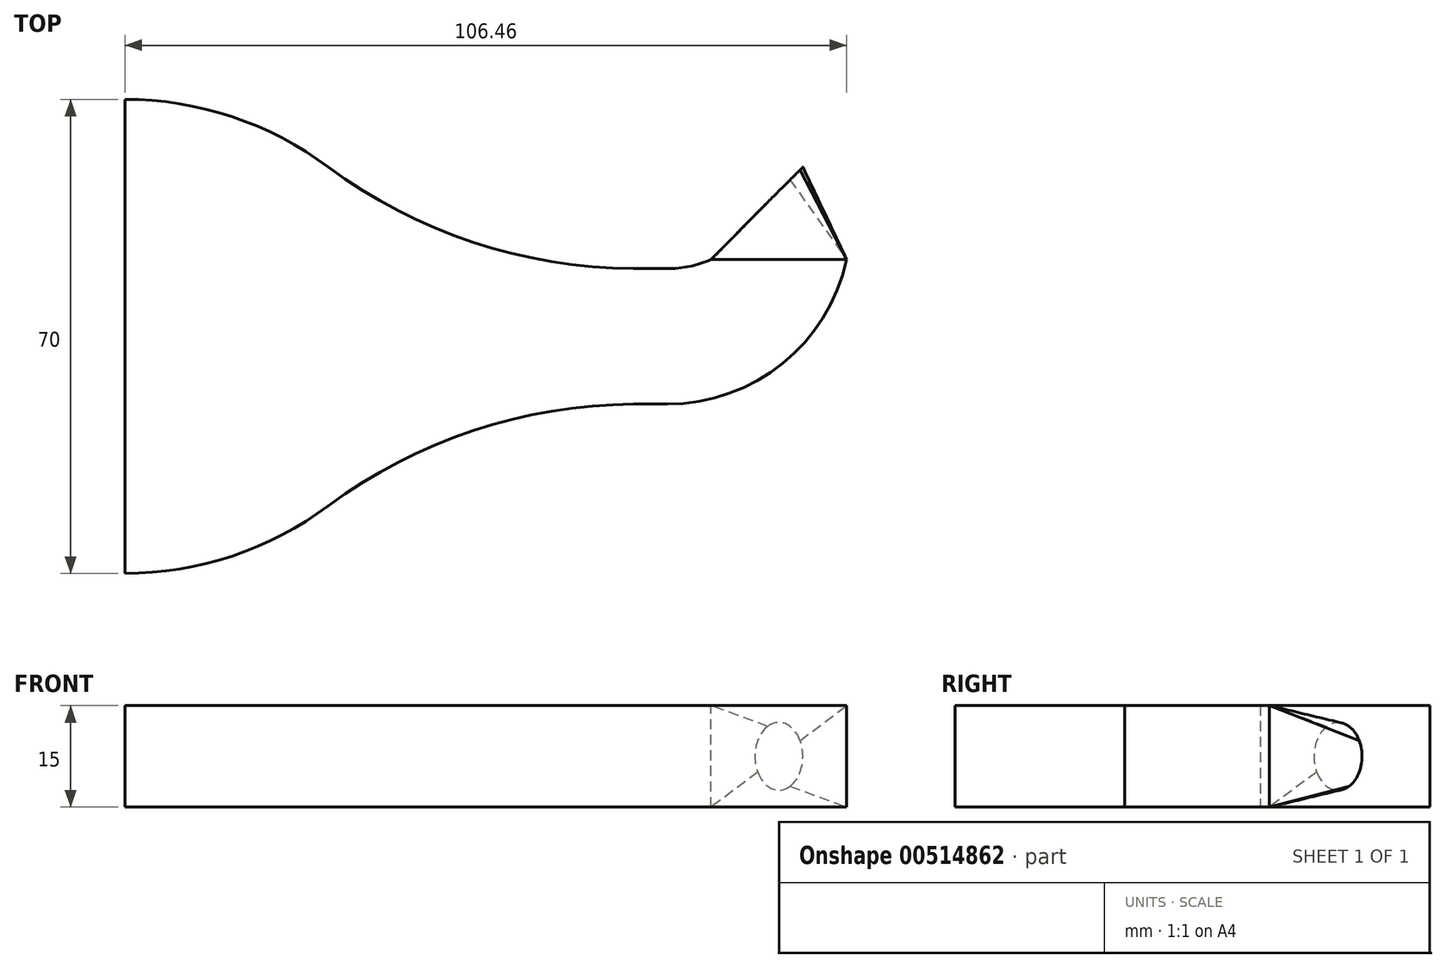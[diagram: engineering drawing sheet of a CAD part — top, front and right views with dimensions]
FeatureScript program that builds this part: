
annotation { "Feature Type Name" : "Feature", "Feature Type Description" : "" }
export const myFeature = defineFeature(function(context is Context, id is Id, definition is map)
    precondition{}
    {
        {
            var Q0;
            Q0=qCreatedBy(makeId("Top.planeOp"),FACE);
            var sketch = newSketch(context, id + "F0", { "sketchPlane" : qUnion([Q0])});
            skLineSegment(sketch, "E0.left", {"start": v(-50, 50) * mm, "end": v(-50, -50) * mm});
            skPoint(sketch, "E0.middle", {"position": v(0, 0) * mm});
            skLineSegment(sketch, "E1", {"start": v(-50, 50) * mm, "end": v(-50, 40) * mm});
            skLineSegment(sketch, "E2", {"start": v(50, 40) * mm, "end": v(42.93, 32.93) * mm});
            skLineSegment(sketch, "E3", {"start": v(42.93, 32.93) * mm, "end": v(46.46, 36.46) * mm});
            skLineSegment(sketch, "E4", {"start": v(-50, 0) * mm, "end": v(-50, -10) * mm});
            skLineSegment(sketch, "E5", {"start": v(-50, -10) * mm, "end": v(-50, 15) * mm});
            skLineSegment(sketch, "E6", {"start": v(-50, 15) * mm, "end": v(114.78, 15) * mm});
            skLineSegment(sketch, "E7", {"start": v(42.93, 32.93) * mm, "end": v(42.93, -37.04) * mm});
            skLineSegment(sketch, "E8", {"start": v(-50, 15) * mm, "end": v(30, 15) * mm});
            skLineSegment(sketch, "E9", {"start": v(30, 15) * mm, "end": v(30, 30) * mm});
            skLineSegment(sketch, "E10", {"start": v(30, 15) * mm, "end": v(30, 0) * mm});
            skLineSegment(sketch, "E11", {"start": v(42.93, 32.93) * mm, "end": v(81, 32.93) * mm});
            skLineSegment(sketch, "E12", {"start": v(46.46, 36.46) * mm, "end": v(46.46, 32.93) * mm});
            skLineSegment(sketch, "E13", {"start": v(46.46, 36.46) * mm, "end": v(46.46, 0) * mm});
            skLineSegment(sketch, "E14", {"start": v(46.46, 36.46) * mm, "end": v(62.14, 20.79) * mm});
            skLineSegment(sketch, "E15", {"start": v(-50, 50) * mm, "end": v(-109.66, 50) * mm});
            skLineSegment(sketch, "E16", {"start": v(-50, 40) * mm, "end": v(-110.5, 40) * mm});
            skLineSegment(sketch, "E17", {"start": v(-50, 15) * mm, "end": v(-113.83, 15) * mm});
            skLineSegment(sketch, "E18", {"start": v(-50, 0) * mm, "end": v(-113, 0) * mm});
            skLineSegment(sketch, "E19", {"start": v(-50, -10) * mm, "end": v(-113, -10) * mm});
            skLineSegment(sketch, "E20", {"start": v(-50, -50) * mm, "end": v(-111.33, -50) * mm});
            skLineSegment(sketch, "E21", {"start": v(30, 30) * mm, "end": v(95.7, 30) * mm});
            skPoint(sketch, "E22", {"position": v(42.93, 30) * mm});
            skPoint(sketch, "E23", {"position": v(46.46, 30) * mm});
            skPoint(sketch, "E24", {"position": v(42.93, 26.34) * mm});
            skLineSegment(sketch, "E25", {"start": v(30, 15) * mm, "end": v(30, 7.5) * mm});
            skLineSegment(sketch, "E26", {"start": v(30, 15) * mm, "end": v(30, 22.5) * mm});
            skLineSegment(sketch, "E27", {"start": v(30, 15) * mm, "end": v(0, 15) * mm});
            skLineSegment(sketch, "E28", {"start": v(-50, 15) * mm, "end": v(-30, 15) * mm});
            skLineSegment(sketch, "E29", {"start": v(-30, 15) * mm, "end": v(-10, 15) * mm});
            skLineSegment(sketch, "E30", {"start": v(-10, 15) * mm, "end": v(10, 15) * mm});
            skSolve(sketch);
        }
        {
            var Q0;
            Q0=sQuery(id+"F0.wireOp",EDGE,"E2");
            cPlane(context, id + "F1", {"entities" : qUnion([Q0]), "cplaneType" : CPlaneType.LINE_ANGLE, "offset" : 25 * mm, "angle" : 90 * degree, "width" : 150 * mm, "height" : 150 * mm});
        }
        {
            var Q0;
            Q0=qCreatedBy(id+"F1.planeOp",FACE);
            var sketch = newSketch(context, id + "F2", { "sketchPlane" : qUnion([Q0])});
            skCircle(sketch, "E31", {"center": v(58.64, 0) * mm, "radius": 5 * mm});
            skSolve(sketch);
        }
        {
            var Q0;
            Q0=sQuery(id+"F0.wireOp",VERTEX,"E6.start");
            var Q1;
            Q1=qCreatedBy(makeId("Right.planeOp"),FACE);
            cPlane(context, id + "F3", {"entities" : qUnion([Q0, Q1]), "cplaneType" : CPlaneType.PLANE_POINT, "offset" : 25 * mm, "width" : 150 * mm, "height" : 150 * mm});
        }
        {
            var Q0;
            Q0=qCreatedBy(id+"F3.planeOp",FACE);
            var sketch = newSketch(context, id + "F4", { "sketchPlane" : qUnion([Q0])});
            skPoint(sketch, "E32", {"position": v(15, 0) * mm});
            skLineSegment(sketch, "E33", {"start": v(50, 10) * mm, "end": v(-20, 10) * mm});
            skLineSegment(sketch, "E34", {"start": v(50, -10) * mm, "end": v(-20, -10) * mm});
            skLineSegment(sketch, "E35", {"start": v(50, 10) * mm, "end": v(50, -10) * mm});
            skLineSegment(sketch, "E36", {"start": v(-20, 10) * mm, "end": v(-20, -10) * mm});
            skLineSegment(sketch, "E37", {"start": v(-49.86, 0) * mm, "end": v(-49.86, 10) * mm});
            skLineSegment(sketch, "E38", {"start": v(-49.86, 0) * mm, "end": v(-49.86, -10) * mm});
            skLineSegment(sketch, "E39", {"start": v(-49.86, 10) * mm, "end": v(-32.86, 10) * mm});
            skLineSegment(sketch, "E40", {"start": v(-32.86, 10) * mm, "end": v(-32.86, -10) * mm});
            skLineSegment(sketch, "E41", {"start": v(-32.86, -10) * mm, "end": v(-49.86, -10) * mm});
            skPoint(sketch, "E42", {"position": v(-32.86, 0) * mm});
            skSolve(sketch);
        }
        {
            var Q0;
            Q0=qCreatedBy(makeId("Front.planeOp"),FACE);
            var Q1;
            Q1=sQuery(id+"F0.wireOp",VERTEX,"E24");
            cPlane(context, id + "F5", {"entities" : qUnion([Q0, Q1]), "cplaneType" : CPlaneType.PLANE_POINT, "offset" : 25 * mm, "width" : 150 * mm, "height" : 150 * mm});
        }
        {
            var Q0;
            Q0=qCreatedBy(id+"F5.planeOp",FACE);
            var sketch = newSketch(context, id + "F6", { "sketchPlane" : qUnion([Q0])});
            skPoint(sketch, "E43", {"position": v(46.46, 0) * mm});
            skLineSegment(sketch, "E44.bottom", {"start": v(36.46, -7.5) * mm, "end": v(56.46, -7.5) * mm});
            skLineSegment(sketch, "E44.top", {"start": v(36.46, 7.5) * mm, "end": v(56.46, 7.5) * mm});
            skLineSegment(sketch, "E44.left", {"start": v(36.46, -7.5) * mm, "end": v(36.46, 7.5) * mm});
            skLineSegment(sketch, "E44.right", {"start": v(56.46, -7.5) * mm, "end": v(56.46, 7.5) * mm});
            skSolve(sketch);
        }
        {
            var Q0;
            Q0=makeQuery(id+"F2.imprint","IMPRINT",FACE,{"disambiguationData":[TD([[makeQuery(id+"F2.imprint","IMPRINT",EDGE,{"derivedFrom":sQuery(id+"F2.wireOp",EDGE,"E31")}),1.0]])]});
            var Q1;
            Q1=makeQuery(id+"F6.imprint","IMPRINT",FACE,{"disambiguationData":[TD([[makeQuery(id+"F6.imprint","IMPRINT",EDGE,{"derivedFrom":sQuery(id+"F6.wireOp",EDGE,"E44.bottom")}),1.0]])]});
            loft(context, id + "F7", {"sheetProfilesArray" : [{ "sheetProfileEntities" : qUnion([Q0]) }, { "sheetProfileEntities" : qUnion([Q1]) }]});
        }
        {
            var Q0;
            Q0=sQuery(id+"F0.wireOp",VERTEX,"E17.start");
            var Q1;
            Q1=qCreatedBy(makeId("Right.planeOp"),FACE);
            cPlane(context, id + "F8", {"entities" : qUnion([Q0, Q1]), "cplaneType" : CPlaneType.PLANE_POINT, "offset" : 25 * mm, "width" : 150 * mm, "height" : 150 * mm});
        }
        {
            var Q0;
            Q0=qCreatedBy(makeId("Top.planeOp"),FACE);
            var Q1;
            Q1=sQuery(id+"F6.wireOp",VERTEX,"E43");
            cPlane(context, id + "F9", {"entities" : qUnion([Q0, Q1]), "cplaneType" : CPlaneType.PLANE_POINT, "offset" : 25 * mm, "width" : 150 * mm, "height" : 150 * mm});
        }
        {
            var Q0;
            Q0=qCreatedBy(id+"F9.planeOp",FACE);
            var sketch = newSketch(context, id + "F10", { "sketchPlane" : qUnion([Q0])});
            skLineSegment(sketch, "E45", {"start": v(38.96, 26.34) * mm, "end": v(53.96, 26.34) * mm});
            skPoint(sketch, "E46", {"position": v(30, 25) * mm});
            skPoint(sketch, "E47", {"position": v(30, 5) * mm});
            skLineSegment(sketch, "E48", {"start": v(38.96, 26.34) * mm, "end": v(36.46, 26.34) * mm});
            skLineSegment(sketch, "E49", {"start": v(53.96, 26.34) * mm, "end": v(56.46, 26.34) * mm});
            skLineSegment(sketch, "E50", {"start": v(30, 25) * mm, "end": v(30, 5) * mm});
            skLineSegment(sketch, "E51", {"start": v(30, 25) * mm, "end": v(25.93, 25) * mm});
            skLineSegment(sketch, "E52", {"start": v(30, 5) * mm, "end": v(25.48, 5) * mm});
            skArc(sketch, "E53", {"start": v(30, 25) * mm, "mid": v(33.3, 25.34) * mm, "end": v(36.46, 26.34) * mm});
            skArc(sketch, "E54", {"start": v(30, 5) * mm, "mid": v(47, 11) * mm, "end": v(56.46, 26.34) * mm});
            skSolve(sketch);
        }
        {
            var Q0;
            Q0=makeQuery(id+"F10.imprint","IMPRINT",FACE,{"disambiguationData":[TD([[makeQuery(id+"F10.imprint","IMPRINT",EDGE,{"derivedFrom":sQuery(id+"F10.wireOp",EDGE,"E45")}),-1.0]])]});
            extrude(context, id + "F11", {"entities" : qUnion([Q0]), "operationType" : NewBodyOperationType.ADD, "endBound" : BoundingType.SYMMETRIC, "depth" : 15 * mm, "offsetDistance" : 25 * mm});
        }
        {
            var Q0;
            Q0=qCreatedBy(makeId("Top.planeOp"),FACE);
            var sketch = newSketch(context, id + "F12", { "sketchPlane" : qUnion([Q0])});
            skPoint(sketch, "E55", {"position": v(30, 25) * mm});
            skPoint(sketch, "E56", {"position": v(-50, 50) * mm});
            skPoint(sketch, "E57", {"position": v(-50, -20) * mm});
            skLineSegment(sketch, "E58", {"start": v(-50, 50) * mm, "end": v(-56.58, 50) * mm});
            skLineSegment(sketch, "E59", {"start": v(-50, -20) * mm, "end": v(-57.7, -20) * mm});
            skLineSegment(sketch, "E60", {"start": v(30, 25) * mm, "end": v(25, 25) * mm});
            skPoint(sketch, "E61", {"position": v(-50, 40) * mm});
            skPoint(sketch, "E62", {"position": v(-50, 15) * mm});
            skPoint(sketch, "E63", {"position": v(-50, 0) * mm});
            skPoint(sketch, "E64", {"position": v(-50, -10) * mm});
            skLineSegment(sketch, "E65.MirrorCS", {"start": v(30, 5) * mm, "end": v(25, 5) * mm});
            skLineSegment(sketch, "E66", {"start": v(-50, 50) * mm, "end": v(-50, -20) * mm});
            skPoint(sketch, "E67", {"position": v(25, 15) * mm});
            skLineSegment(sketch, "E68", {"start": v(25, 15) * mm, "end": v(-20, 15) * mm});
            skLineSegment(sketch, "E69", {"start": v(-50, 40) * mm, "end": v(-20, 40) * mm});
            skArc(sketch, "E70", {"start": v(-20, 40) * mm, "mid": v(-34.19, 47.43) * mm, "end": v(-50, 50) * mm});
            skLineSegment(sketch, "E71", {"start": v(-20, 40) * mm, "end": v(-20, 40) * mm});
            skArc(sketch, "E72", {"start": v(-20, 40) * mm, "mid": v(1.3, 28.93) * mm, "end": v(25, 25) * mm});
            skArc(sketch, "E73.MirrorCS", {"start": v(-20, -10) * mm, "mid": v(-34.19, -17.43) * mm, "end": v(-50, -20) * mm});
            skArc(sketch, "E74.MirrorCS", {"start": v(-20, -10) * mm, "mid": v(1.3, 1.07) * mm, "end": v(25, 5) * mm});
            skPoint(sketch, "E75", {"position": v(10, 15) * mm});
            skPoint(sketch, "E76", {"position": v(-50, -50) * mm});
            skLineSegment(sketch, "E77", {"start": v(-50, -20) * mm, "end": v(-50, -24.93) * mm});
            skLineSegment(sketch, "E78", {"start": v(-50, -24.93) * mm, "end": v(-42.8, -24.93) * mm});
            skLineSegment(sketch, "E79", {"start": v(-20, -10) * mm, "end": v(-22.21, -11.7) * mm});
            skLineSegment(sketch, "E80", {"start": v(-50, -50) * mm, "end": v(-61.6, -50) * mm});
            skLineSegment(sketch, "E81", {"start": v(-50, 15) * mm, "end": v(-50, 24) * mm});
            skLineSegment(sketch, "E82", {"start": v(-50, 15) * mm, "end": v(-50, 6) * mm});
            skLineSegment(sketch, "E83", {"start": v(-50, -20) * mm, "end": v(-50, 5) * mm});
            skLineSegment(sketch, "E84", {"start": v(-50, 50) * mm, "end": v(-50, 25) * mm});
            skLineSegment(sketch, "E85", {"start": v(-50, -20) * mm, "end": v(-18.93, -20) * mm});
            skPoint(sketch, "E86", {"position": v(30, 5) * mm});
            skLineSegment(sketch, "E87", {"start": v(30, 25) * mm, "end": v(30, 5) * mm});
            skSolve(sketch);
        }
        {
            var Q0;
            Q0=makeQuery(id+"F12.imprint","IMPRINT",FACE,{"disambiguationData":[TD([[makeQuery(id+"F12.imprint","IMPRINT",EDGE,{"derivedFrom":sQuery(id+"F12.wireOp",EDGE,"E60")}),1.0]])]});
            extrude(context, id + "F13", {"entities" : qUnion([Q0]), "operationType" : NewBodyOperationType.ADD, "endBound" : BoundingType.SYMMETRIC, "depth" : 15 * mm, "offsetDistance" : 25 * mm});
        }
        {
            var Q0;
            {var subQ2=sQuery(id+"F12.wireOp",EDGE,"E69");Q0=makeQuery(id+"F12.imprint","IMPRINT",FACE,{"disambiguationData":[TD([[makeQuery(id+"F12.imprint","IMPRINT",EDGE,{"derivedFrom":subQ2}),1.0]])]});}
            var Q1;
            {var subQ0=sQuery(id+"F12.wireOp",EDGE,"E69");Q1=makeQuery(id+"F12.imprint","IMPRINT",FACE,{"disambiguationData":[TD([[makeQuery(id+"F12.imprint","IMPRINT",EDGE,{"derivedFrom":subQ0}),-1.0]])]});}
            var Q2;
            {var subQ6=sQuery(id+"F12.wireOp",EDGE,"O4udIbtW-wG9n-ZYI7-Cbfw-suRvEkwaG2LF");Q2=makeQuery(id+"F12.imprint","IMPRINT",FACE,{"disambiguationData":[TD([[makeQuery(id+"F12.imprint","IMPRINT",EDGE,{"derivedFrom":subQ6}),-1.0]])]});}
            var Q3;
            {var subQ5=sQuery(id+"F12.wireOp",EDGE,"sRJjo6lo-ZlNL-p5sG-CHF8-b8NFd7EilJaZ");Q3=makeQuery(id+"F12.imprint","IMPRINT",FACE,{"disambiguationData":[TD([[makeQuery(id+"F12.imprint","IMPRINT",EDGE,{"derivedFrom":subQ5}),-1.0]])]});}
            var Q4;
            {var subQ4=sQuery(id+"F12.wireOp",EDGE,"E73.MirrorCS");Q4=makeQuery(id+"F12.imprint","IMPRINT",FACE,{"disambiguationData":[TD([[makeQuery(id+"F12.imprint","IMPRINT",EDGE,{"derivedFrom":subQ4}),-1.0]])]});}
            extrude(context, id + "F14", {"entities" : qUnion([Q0, Q1, Q2, Q3, Q4]), "operationType" : NewBodyOperationType.ADD, "endBound" : BoundingType.SYMMETRIC, "depth" : 15 * mm, "offsetDistance" : 25 * mm});
        }
    });
